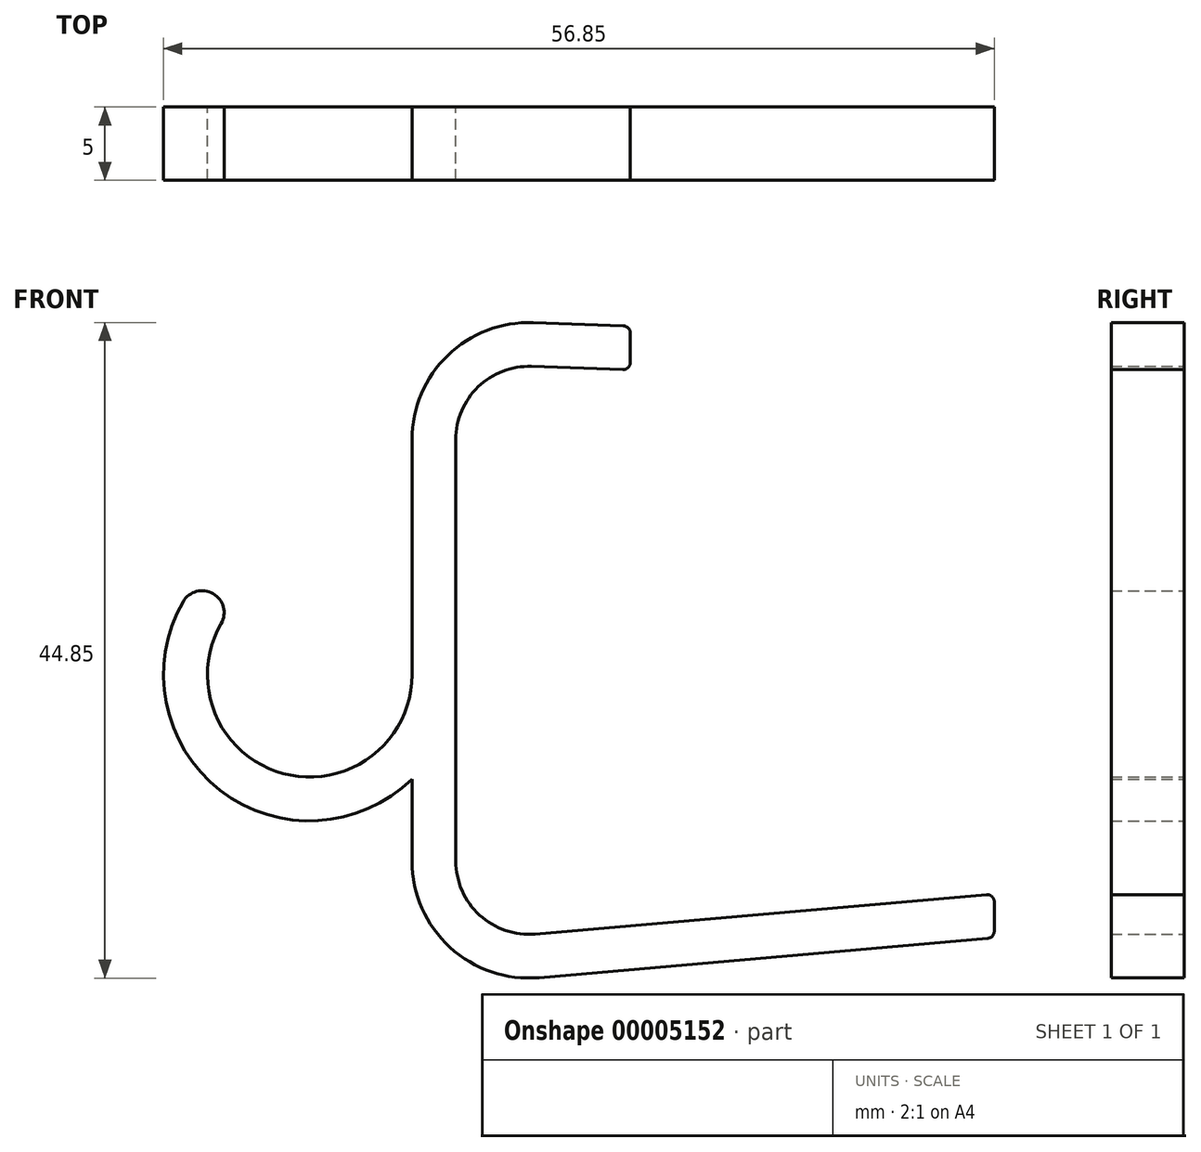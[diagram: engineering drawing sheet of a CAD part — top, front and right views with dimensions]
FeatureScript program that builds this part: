
annotation { "Feature Type Name" : "Feature", "Feature Type Description" : "" }
export const myFeature = defineFeature(function(context is Context, id is Id, definition is map)
    precondition{}
    {
        {
            var Q0;
            Q0=qCreatedBy(makeId("Front.planeOp"),FACE);
            var sketch = newSketch(context, id + "F0", { "sketchPlane" : qUnion([Q0])});
            skLineSegment(sketch, "E0", {"start": v(-0.54, -0.05) * mm, "end": v(-31.41, -2.75) * mm});
            skLineSegment(sketch, "E1", {"start": v(-36.85, 2.23) * mm, "end": v(-36.85, 31.1) * mm});
            skLineSegment(sketch, "E2", {"start": v(-31.67, 36.1) * mm, "end": v(-25.42, 35.88) * mm});
            skLineSegment(sketch, "E3", {"start": v(-24.9, 36.38) * mm, "end": v(-24.9, 38.37) * mm});
            skLineSegment(sketch, "E4", {"start": v(-25.39, 38.87) * mm, "end": v(-31.57, 39.09) * mm});
            skLineSegment(sketch, "E5", {"start": v(-39.85, 31.1) * mm, "end": v(-39.85, 15) * mm});
            skLineSegment(sketch, "E6", {"start": v(-31.15, -5.73) * mm, "end": v(-0.46, -3.04) * mm});
            skLineSegment(sketch, "E7", {"start": v(0, -2.54) * mm, "end": v(0, -0.55) * mm});
            skPoint(sketch, "E8.visualSharp", {"position": v(-36.85, -3.22) * mm});
            skArc(sketch, "E8.filletArc", {"start": v(-36.85, 2.23) * mm, "mid": v(-35.23, -1.45) * mm, "end": v(-31.41, -2.75) * mm});
            skPoint(sketch, "E9.visualSharp", {"position": v(-36.85, 36.28) * mm});
            skArc(sketch, "E9.filletArc", {"start": v(-31.67, 36.1) * mm, "mid": v(-35.32, 34.7) * mm, "end": v(-36.85, 31.1) * mm});
            skPoint(sketch, "E10.visualSharp", {"position": v(-39.85, 39.38) * mm});
            skArc(sketch, "E10.filletArc", {"start": v(-31.57, 39.09) * mm, "mid": v(-37.4, 36.85) * mm, "end": v(-39.85, 31.1) * mm});
            skPoint(sketch, "E11.visualSharp", {"position": v(-39.85, -6.49) * mm});
            skArc(sketch, "E11.filletArc", {"start": v(-39.85, 2.24) * mm, "mid": v(-37.25, -3.65) * mm, "end": v(-31.15, -5.73) * mm});
            skPoint(sketch, "E12.visualSharp", {"position": v(0, -3) * mm});
            skArc(sketch, "E12.filletArc", {"start": v(-0.46, -3.04) * mm, "mid": v(-0.13, -2.88) * mm, "end": v(0, -2.54) * mm});
            skPoint(sketch, "E13.visualSharp", {"position": v(0, 0) * mm});
            skArc(sketch, "E13.filletArc", {"start": v(0, -0.55) * mm, "mid": v(-0.16, -0.18) * mm, "end": v(-0.54, -0.05) * mm});
            skPoint(sketch, "E14.visualSharp", {"position": v(-24.9, 35.86) * mm});
            skArc(sketch, "E14.filletArc", {"start": v(-25.42, 35.88) * mm, "mid": v(-25.06, 36.02) * mm, "end": v(-24.9, 36.38) * mm});
            skPoint(sketch, "E15.visualSharp", {"position": v(-24.9, 38.86) * mm});
            skArc(sketch, "E15.filletArc", {"start": v(-24.9, 38.37) * mm, "mid": v(-25.05, 38.72) * mm, "end": v(-25.39, 38.87) * mm});
            skArc(sketch, "E16", {"start": v(-52.9, 18.5) * mm, "mid": v(-48.66, 8.24) * mm, "end": v(-39.85, 15) * mm});
            skLineSegment(sketch, "E17", {"start": v(-52.9, 18.5) * mm, "end": v(-46.85, 15) * mm, "construction": true});
            skLineSegment(sketch, "E18", {"start": v(-46.85, 15) * mm, "end": v(-39.85, 15) * mm, "construction": true});
            skArc(sketch, "E19.0", {"start": v(-55.5, 20) * mm, "mid": v(-52.97, 7.1) * mm, "end": v(-39.85, 7.86) * mm});
            skLineSegment(sketch, "E20.trimOffspring", {"start": v(-39.85, 7.86) * mm, "end": v(-39.85, 2.24) * mm});
            skArc(sketch, "E21", {"start": v(-52.9, 18.5) * mm, "mid": v(-53.46, 20.55) * mm, "end": v(-55.5, 20) * mm});
            skSolve(sketch);
        }
        {
            var Q0;
            Q0 = qSketchRegion(id + "F0", true);
            extrude(context, id + "F1", {"entities" : qUnion([Q0]), "depth" : 5 * mm});
        }
    });
